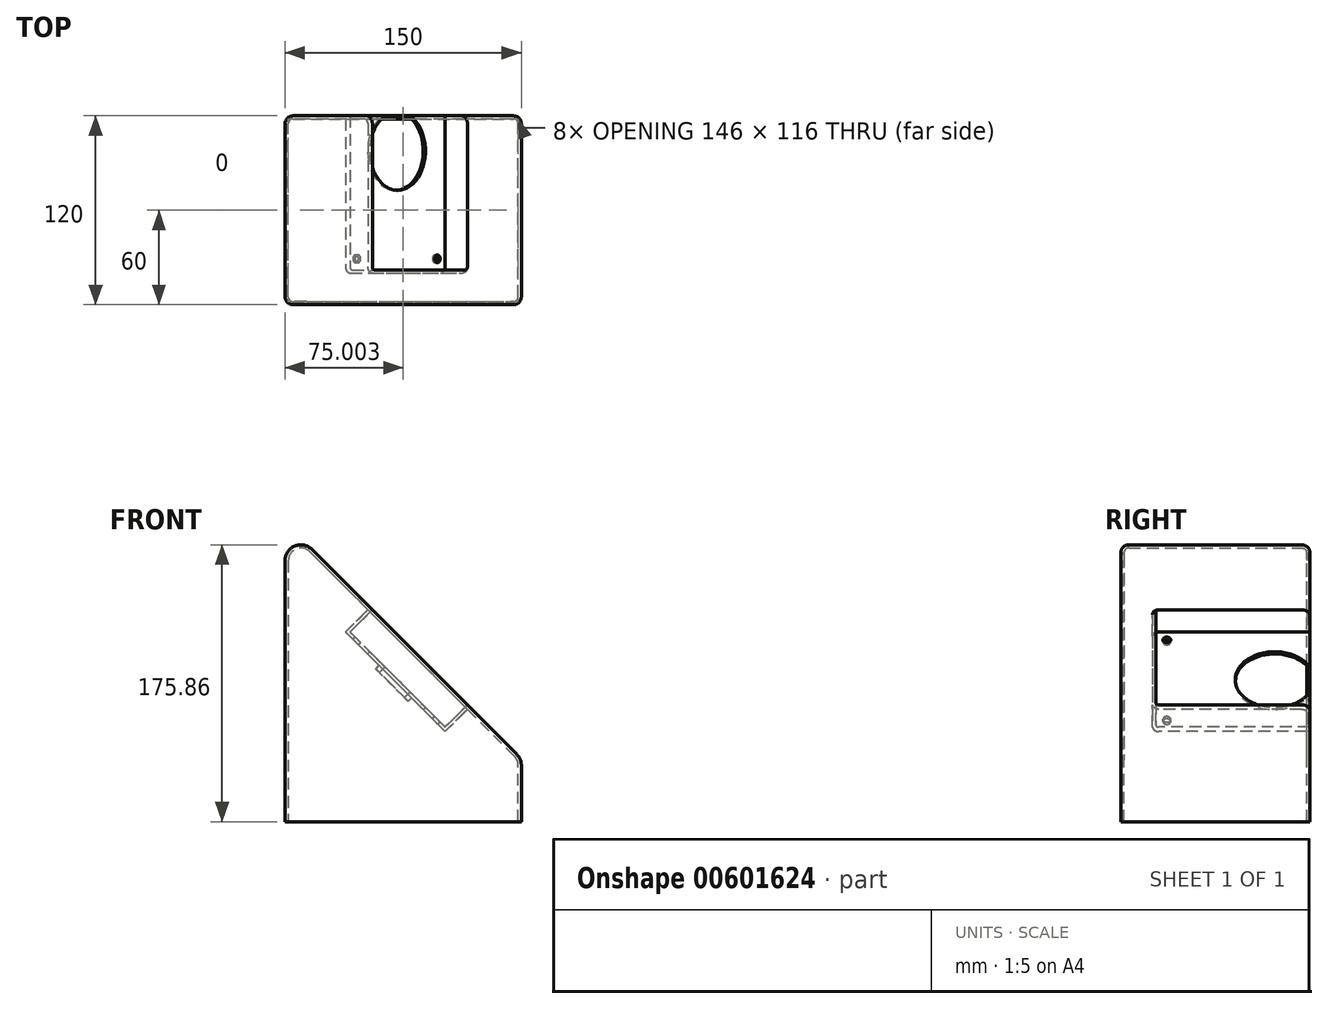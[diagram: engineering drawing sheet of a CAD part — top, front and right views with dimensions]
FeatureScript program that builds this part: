
annotation { "Feature Type Name" : "Feature", "Feature Type Description" : "" }
export const myFeature = defineFeature(function(context is Context, id is Id, definition is map)
    precondition{}
    {
        {
            var Q0;
            Q0=qCreatedBy(makeId("Front.planeOp"),FACE);
            var sketch = newSketch(context, id + "F0", { "sketchPlane" : qUnion([Q0])});
            skLineSegment(sketch, "E0", {"start": v(-84.02, -102.86) * mm, "end": v(65.98, -102.86) * mm});
            skLineSegment(sketch, "E1", {"start": v(65.98, -102.86) * mm, "end": v(65.98, -67) * mm});
            skLineSegment(sketch, "E2", {"start": v(63.05, -59.93) * mm, "end": v(-66.95, 70.07) * mm});
            skLineSegment(sketch, "E3", {"start": v(-84.02, 63) * mm, "end": v(-84.02, -102.86) * mm});
            skPoint(sketch, "E4.visualSharp", {"position": v(-84.02, 87.14) * mm});
            skArc(sketch, "E4.filletArc", {"start": v(-66.95, 70.07) * mm, "mid": v(-77.84, 72.24) * mm, "end": v(-84.02, 63) * mm});
            skPoint(sketch, "E5.visualSharp", {"position": v(65.98, -62.86) * mm});
            skArc(sketch, "E5.filletArc", {"start": v(65.98, -67) * mm, "mid": v(65.22, -63.17) * mm, "end": v(63.05, -59.93) * mm});
            skSolve(sketch);
        }
        {
            var Q0;
            Q0=makeQuery(id+"F0.imprint","IMPRINT",FACE,{"disambiguationData":[TD([[makeQuery(id+"F0.imprint","IMPRINT",EDGE,{"derivedFrom":sQuery(id+"F0.wireOp",EDGE,"E0")}),1.0]])]});
            extrude(context, id + "F1", {"entities" : qUnion([Q0]), "endBound" : BoundingType.SYMMETRIC, "depth" : 120 * mm});
        }
        {
            var Q0;
            Q0=makeQuery(id+"F1.opExtrude","SWEPT_FACE",FACE,{"disambiguationData":[OSD([sQuery(id+"F0.wireOp",EDGE,"E2")])]});
            var sketch = newSketch(context, id + "F2", { "sketchPlane" : qUnion([Q0])});
            skLineSegment(sketch, "E6.bottom", {"start": v(67.66, 42.7) * mm, "end": v(-35.84, 42.7) * mm});
            skLineSegment(sketch, "E6.top", {"start": v(67.66, -42.7) * mm, "end": v(-35.84, -42.7) * mm});
            skLineSegment(sketch, "E6.left", {"start": v(69.66, 40.7) * mm, "end": v(69.66, -40.7) * mm});
            skLineSegment(sketch, "E6.right", {"start": v(-37.84, 40.7) * mm, "end": v(-37.84, -40.7) * mm});
            skPoint(sketch, "E6.middle", {"position": v(15.91, 0) * mm});
            skPoint(sketch, "E7.visualSharp", {"position": v(-37.84, -42.7) * mm});
            skArc(sketch, "E7.filletArc", {"start": v(-37.84, -40.7) * mm, "mid": v(-37.25, -42.11) * mm, "end": v(-35.84, -42.7) * mm});
            skPoint(sketch, "E8.visualSharp", {"position": v(-37.84, 42.7) * mm});
            skArc(sketch, "E8.filletArc", {"start": v(-35.84, 42.7) * mm, "mid": v(-37.25, 42.11) * mm, "end": v(-37.84, 40.7) * mm});
            skPoint(sketch, "E9.visualSharp", {"position": v(69.66, 42.7) * mm});
            skArc(sketch, "E9.filletArc", {"start": v(69.66, 40.7) * mm, "mid": v(69.08, 42.11) * mm, "end": v(67.66, 42.7) * mm});
            skPoint(sketch, "E10.visualSharp", {"position": v(69.66, -42.7) * mm});
            skArc(sketch, "E10.filletArc", {"start": v(67.66, -42.7) * mm, "mid": v(69.08, -42.11) * mm, "end": v(69.66, -40.7) * mm});
            skCircle(sketch, "E11", {"center": v(37.66, 0) * mm, "radius": 25 * mm});
            skCircle(sketch, "E12", {"center": v(-30.84, -35.7) * mm, "radius": 2.5 * mm});
            skCircle(sketch, "E13", {"center": v(-30.84, 35.7) * mm, "radius": 2.5 * mm});
            skCircle(sketch, "E14", {"center": v(62.66, 35.7) * mm, "radius": 2.5 * mm});
            skCircle(sketch, "E15", {"center": v(62.66, -35.7) * mm, "radius": 2.5 * mm});
            skSolve(sketch);
        }
        {
            var Q0;
            Q0=makeQuery(id+"F2.imprint","IMPRINT",FACE,{"disambiguationData":[TD([[makeQuery(id+"F2.imprint","IMPRINT",EDGE,{"derivedFrom":sQuery(id+"F2.wireOp",EDGE,"E6.bottom")}),1.0]])]});
            var Q1;
            Q1=makeQuery(id+"F2.imprint","IMPRINT",FACE,{"disambiguationData":[TD([[makeQuery(id+"F2.imprint","IMPRINT",EDGE,{"derivedFrom":sQuery(id+"F2.wireOp",EDGE,"E11")}),1.0]])]});
            var Q2;
            Q2=makeQuery(id+"F2.imprint","IMPRINT",FACE,{"disambiguationData":[TD([[makeQuery(id+"F2.imprint","IMPRINT",EDGE,{"derivedFrom":sQuery(id+"F2.wireOp",EDGE,"E13")}),1.0]])]});
            var Q3;
            Q3=makeQuery(id+"F2.imprint","IMPRINT",FACE,{"disambiguationData":[TD([[makeQuery(id+"F2.imprint","IMPRINT",EDGE,{"derivedFrom":sQuery(id+"F2.wireOp",EDGE,"E14")}),1.0]])]});
            var Q4;
            Q4=makeQuery(id+"F2.imprint","IMPRINT",FACE,{"disambiguationData":[TD([[makeQuery(id+"F2.imprint","IMPRINT",EDGE,{"derivedFrom":sQuery(id+"F2.wireOp",EDGE,"E15")}),1.0]])]});
            var Q5;
            Q5=makeQuery(id+"F2.imprint","IMPRINT",FACE,{"disambiguationData":[TD([[makeQuery(id+"F2.imprint","IMPRINT",EDGE,{"derivedFrom":sQuery(id+"F2.wireOp",EDGE,"E12")}),1.0]])]});
            extrude(context, id + "F3", {"entities" : qUnion([Q0, Q1, Q2, Q3, Q4, Q5]), "operationType" : NewBodyOperationType.REMOVE, "oppositeDirection" : true, "depth" : 20 * mm});
        }
        {
            var Q0;
            Q0=makeQuery(id+"F1.opExtrude","CAP_EDGE",EDGE,{"disambiguationData":[OSD([sQuery(id+"F0.wireOp",EDGE,"E2")])],"isStart":true});
            var Q1;
            Q1=makeQuery(id+"F1.opExtrude","CAP_EDGE",EDGE,{"disambiguationData":[OSD([sQuery(id+"F0.wireOp",EDGE,"E2")])],"isStart":false});
            fillet(context, id + "F4", {"entities" : qUnion([Q0, Q1]), "radius" : 5 * mm, "tangentPropagation" : true, "allowEdgeOverflow" : false});
        }
        {
            var Q0;
            Q0=makeQuery(id+"F1.opExtrude","SWEPT_FACE",FACE,{"disambiguationData":[OSD([sQuery(id+"F0.wireOp",EDGE,"E0")])]});
            shell(context, id + "F5", {"entities" : qUnion([Q0]), "thickness" : 2 * mm});
        }
        {
            var Q0;
            Q0=makeQuery(id+"F2.imprint","IMPRINT",FACE,{"disambiguationData":[TD([[makeQuery(id+"F2.imprint","IMPRINT",EDGE,{"derivedFrom":sQuery(id+"F2.wireOp",EDGE,"E11")}),1.0]])]});
            var Q1;
            Q1=makeQuery(id+"F2.imprint","IMPRINT",FACE,{"disambiguationData":[TD([[makeQuery(id+"F2.imprint","IMPRINT",EDGE,{"derivedFrom":sQuery(id+"F2.wireOp",EDGE,"E13")}),1.0]])]});
            var Q2;
            Q2=makeQuery(id+"F2.imprint","IMPRINT",FACE,{"disambiguationData":[TD([[makeQuery(id+"F2.imprint","IMPRINT",EDGE,{"derivedFrom":sQuery(id+"F2.wireOp",EDGE,"E12")}),1.0]])]});
            var Q3;
            Q3=makeQuery(id+"F2.imprint","IMPRINT",FACE,{"disambiguationData":[TD([[makeQuery(id+"F2.imprint","IMPRINT",EDGE,{"derivedFrom":sQuery(id+"F2.wireOp",EDGE,"E14")}),1.0]])]});
            var Q4;
            Q4=makeQuery(id+"F2.imprint","IMPRINT",FACE,{"disambiguationData":[TD([[makeQuery(id+"F2.imprint","IMPRINT",EDGE,{"derivedFrom":sQuery(id+"F2.wireOp",EDGE,"E15")}),1.0]])]});
            extrude(context, id + "F6", {"entities" : qUnion([Q0, Q1, Q2, Q3, Q4]), "operationType" : NewBodyOperationType.REMOVE, "oppositeDirection" : true, "depth" : 25 * mm});
        }
    });
